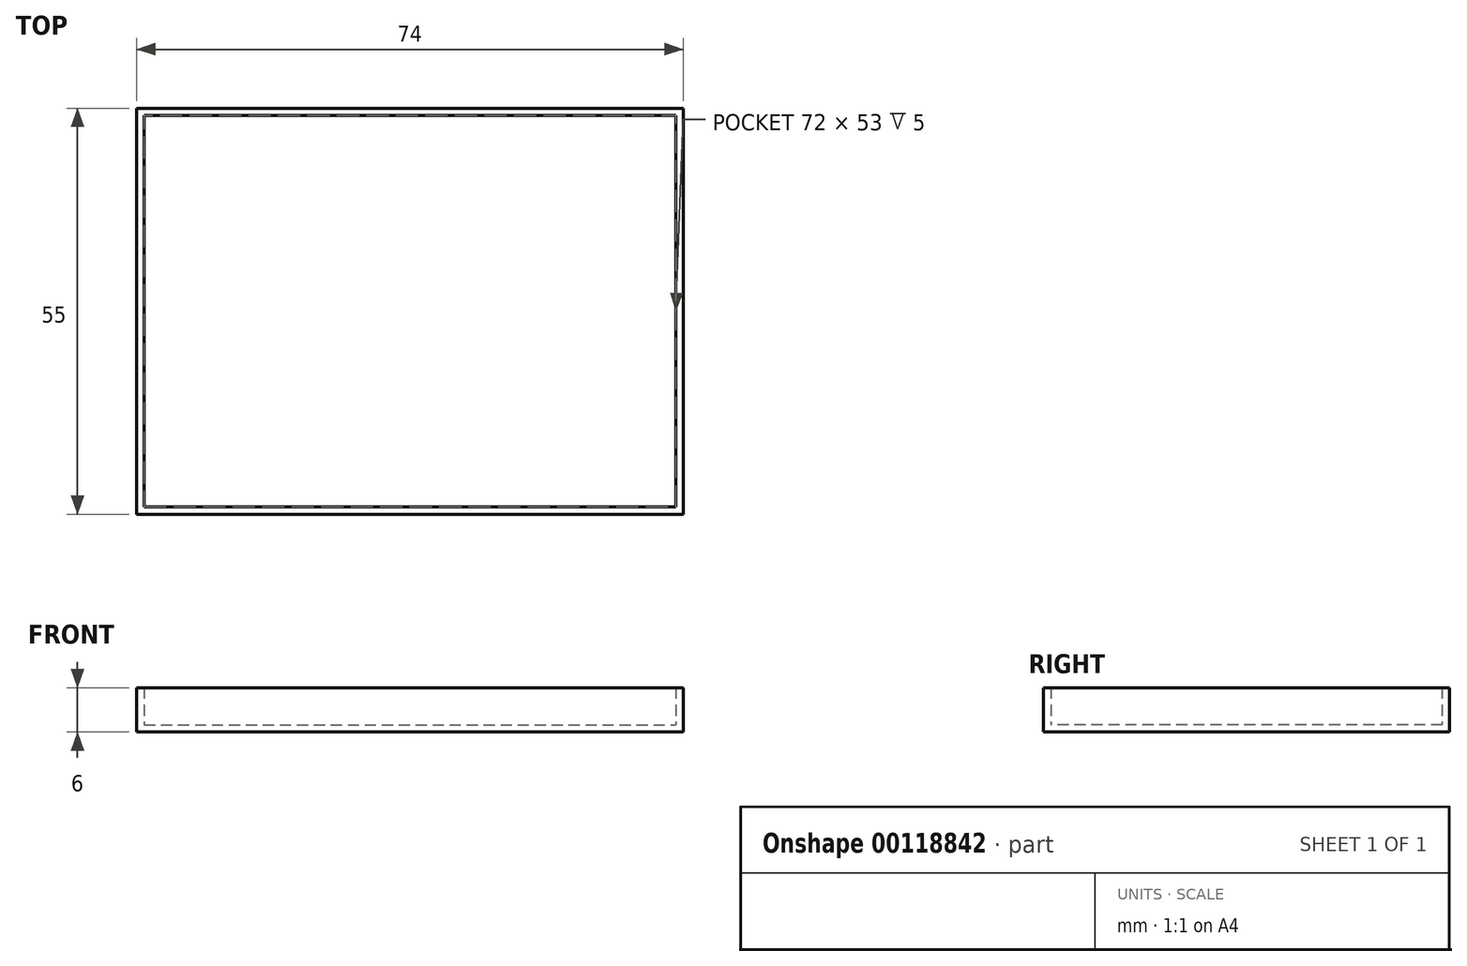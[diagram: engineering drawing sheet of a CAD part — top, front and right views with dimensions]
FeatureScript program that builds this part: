
annotation { "Feature Type Name" : "Feature", "Feature Type Description" : "" }
export const myFeature = defineFeature(function(context is Context, id is Id, definition is map)
    precondition{}
    {
        {
            var Q0;
            Q0=qCreatedBy(makeId("Top.planeOp"),FACE);
            var sketch = newSketch(context, id + "F0", { "sketchPlane" : qUnion([Q0])});
            skLineSegment(sketch, "E0.bottom", {"start": v(-36, 26.5) * mm, "end": v(36, 26.5) * mm});
            skLineSegment(sketch, "E0.top", {"start": v(-36, -26.5) * mm, "end": v(36, -26.5) * mm});
            skLineSegment(sketch, "E0.left", {"start": v(-36, 26.5) * mm, "end": v(-36, -26.5) * mm});
            skLineSegment(sketch, "E0.right", {"start": v(36, 26.5) * mm, "end": v(36, -26.5) * mm});
            skPoint(sketch, "E0.middle", {"position": v(0, 0) * mm});
            skLineSegment(sketch, "E1.0", {"start": v(-37, 27.5) * mm, "end": v(37, 27.5) * mm});
            skLineSegment(sketch, "E1.1", {"start": v(-37, 27.5) * mm, "end": v(-37, -27.5) * mm});
            skLineSegment(sketch, "E1.2", {"start": v(-37, -27.5) * mm, "end": v(37, -27.5) * mm});
            skLineSegment(sketch, "E1.3", {"start": v(37, 27.5) * mm, "end": v(37, -27.5) * mm});
            skSolve(sketch);
        }
        {
            var Q0;
            Q0=makeQuery(id+"F0.imprint","IMPRINT",FACE,{"disambiguationData":[TD([[makeQuery(id+"F0.imprint","IMPRINT",EDGE,{"derivedFrom":sQuery(id+"F0.wireOp",EDGE,"E0.bottom")}),-1.0]])]});
            extrude(context, id + "F1", {"entities" : qUnion([Q0]), "depth" : 1 * mm});
        }
        {
            var Q0;
            Q0 = qSketchRegion(id + "F0", true);
            extrude(context, id + "F2", {"entities" : qUnion([Q0]), "operationType" : NewBodyOperationType.ADD, "depth" : 6 * mm});
        }
    });
